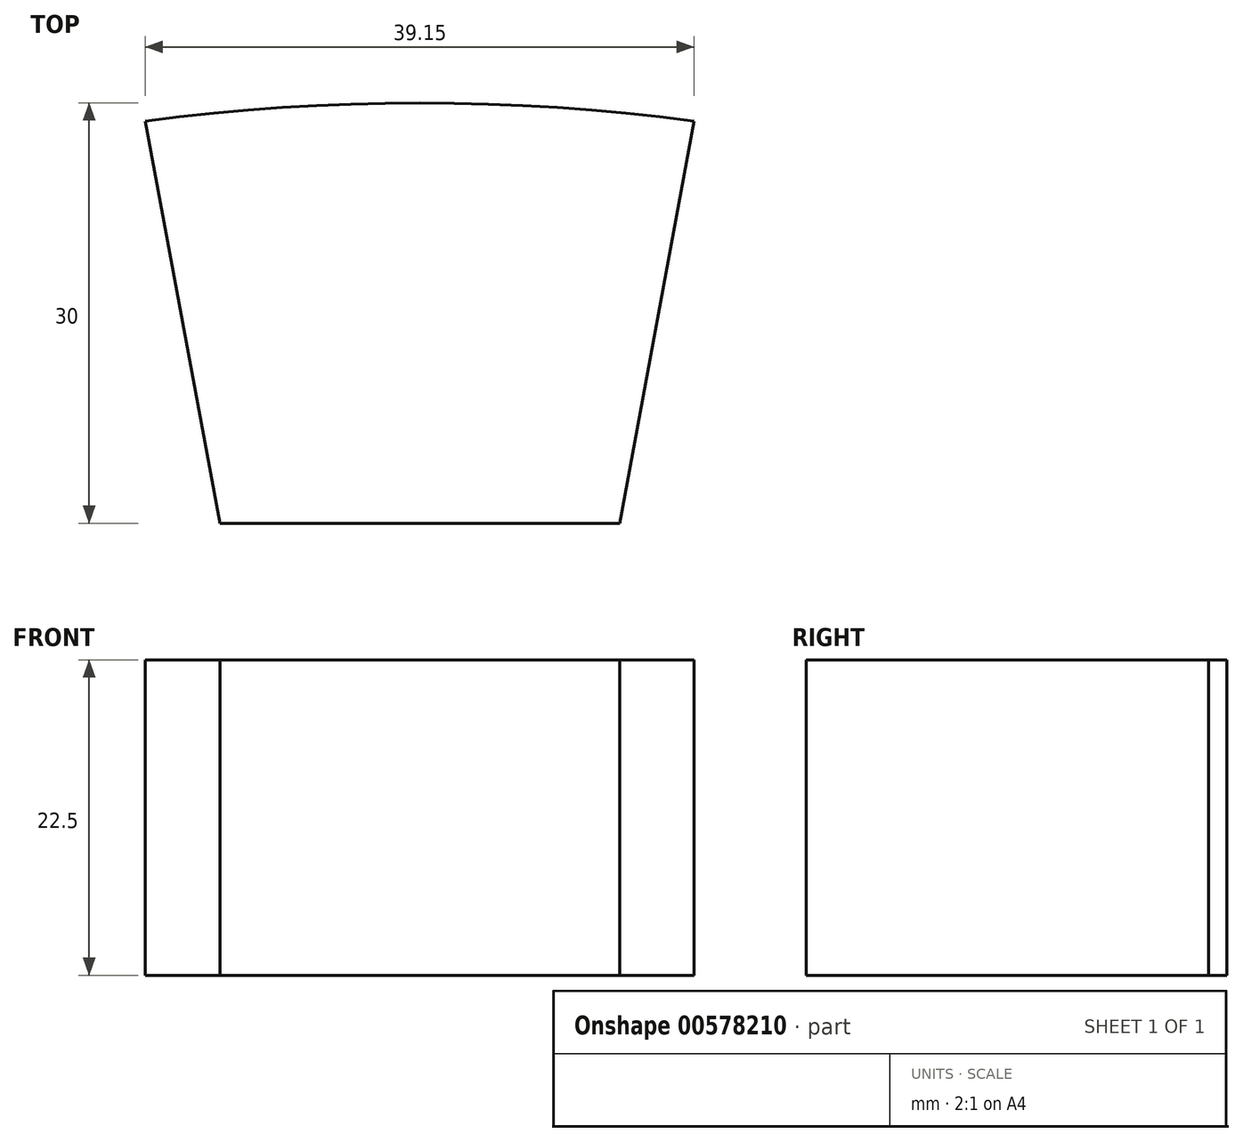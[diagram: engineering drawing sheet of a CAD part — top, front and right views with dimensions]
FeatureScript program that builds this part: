
annotation { "Feature Type Name" : "Feature", "Feature Type Description" : "" }
export const myFeature = defineFeature(function(context is Context, id is Id, definition is map)
    precondition{}
    {
        {
            var Q0;
            Q0=qCreatedBy(makeId("Top.planeOp"),FACE);
            var sketch = newSketch(context, id + "F0", { "sketchPlane" : qUnion([Q0])});
            skLineSegment(sketch, "E0.bottom", {"start": v(14.26, -15) * mm, "end": v(-14.26, -15) * mm});
            skPoint(sketch, "E0.middle", {"position": v(0, 0) * mm});
            skArc(sketch, "E1", {"start": v(19.57, 13.7) * mm, "mid": v(0, 15) * mm, "end": v(-19.57, 13.7) * mm});
            skLineSegment(sketch, "E2", {"start": v(-19.57, 13.7) * mm, "end": v(-14.26, -15) * mm});
            skLineSegment(sketch, "E3", {"start": v(19.58, 13.7) * mm, "end": v(14.26, -15) * mm});
            skPoint(sketch, "E4.orphan", {"position": v(-19.57, -15) * mm});
            skPoint(sketch, "E5.orphan", {"position": v(19.58, -15) * mm});
            skPoint(sketch, "E0.right.end.orphan", {"position": v(-19.57, 15) * mm});
            skPoint(sketch, "E0.left.end.orphan", {"position": v(19.57, 15) * mm});
            skSolve(sketch);
        }
        {
            var Q0;
            Q0=qSketchRegion(id+"F0",true);
            extrude(context, id + "F1", {"entities" : qUnion([Q0]), "depth" : 22.5 * mm, "offsetDistance" : 25 * mm});
        }
    });
